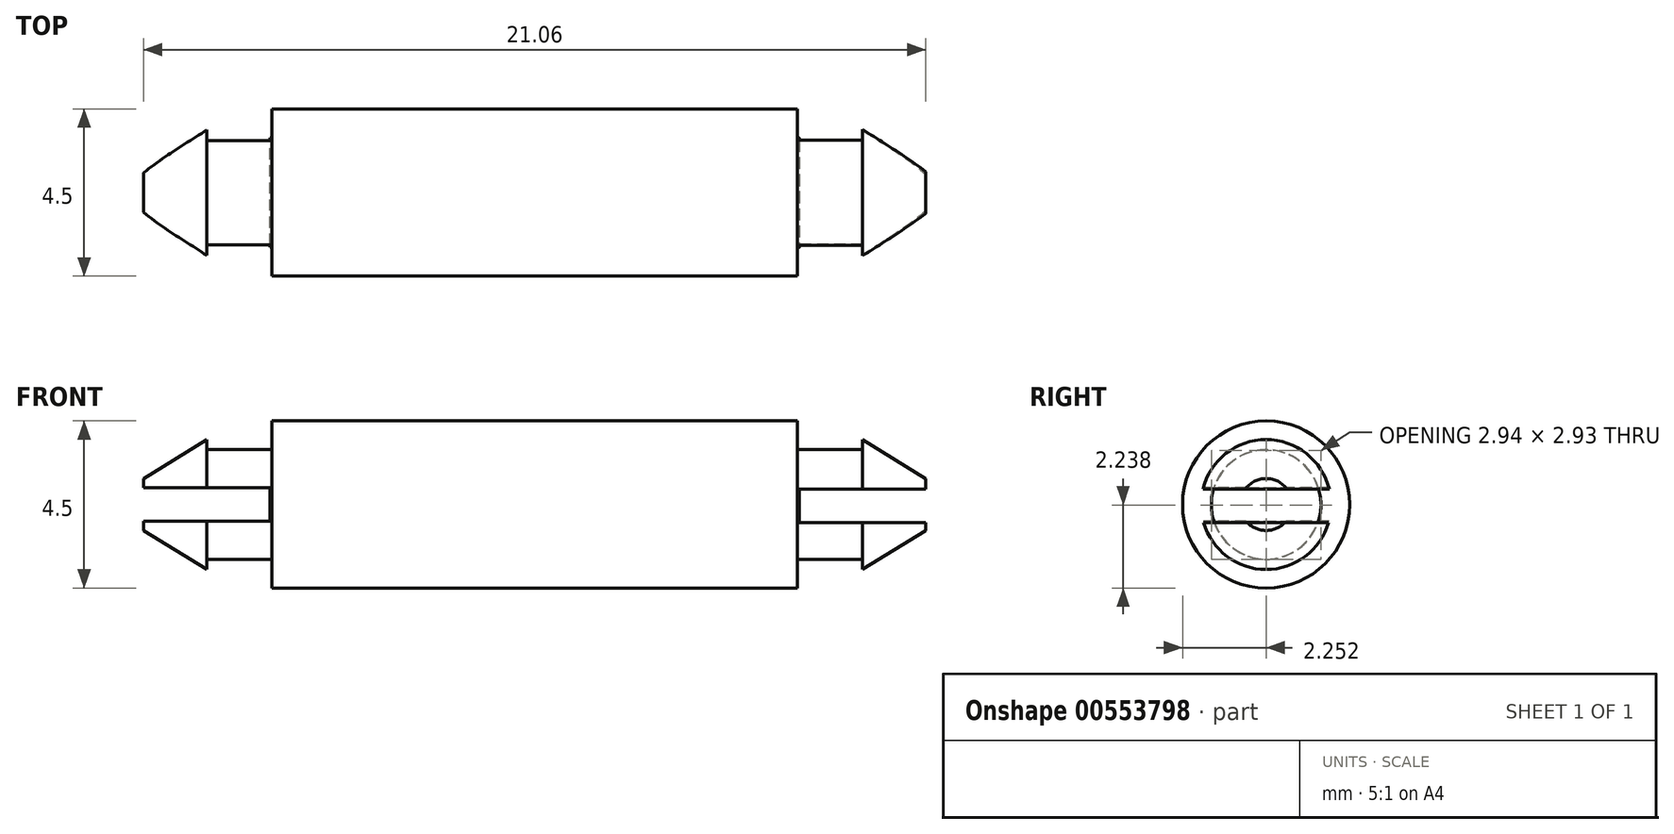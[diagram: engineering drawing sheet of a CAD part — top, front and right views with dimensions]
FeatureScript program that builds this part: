
annotation { "Feature Type Name" : "Feature", "Feature Type Description" : "" }
export const myFeature = defineFeature(function(context is Context, id is Id, definition is map)
    precondition{}
    {
        {
            var Q0;
            Q0=qCreatedBy(makeId("Right.planeOp"),FACE);
            var sketch = newSketch(context, id + "F0", { "sketchPlane" : qUnion([Q0])});
            skCircle(sketch, "E0", {"center": v(0, 0) * mm, "radius": 2.25 * mm});
            skCircle(sketch, "E1", {"center": v(0, 0) * mm, "radius": 1.48 * mm});
            skSolve(sketch);
        }
        {
            var Q0;
            Q0=makeQuery(id+"F0.imprint","IMPRINT",FACE,{"disambiguationData":[TD([[makeQuery(id+"F0.imprint","IMPRINT",EDGE,{"derivedFrom":sQuery(id+"F0.wireOp",EDGE,"E0")}),1.0]])]});
            var Q1;
            Q1 = qSketchRegion(id + "FBEnAiZPMkB544y_1", true);
            extrude(context, id + "F1", {"entities" : qUnion([Q0, Q1]), "endBound" : BoundingType.SYMMETRIC, "depth" : 14.15 * mm, "offsetDistance" : 25 * mm});
        }
        {
            var Q0;
            Q0=makeQuery(id+"F0.imprint","IMPRINT",FACE,{"disambiguationData":[TD([[makeQuery(id+"F0.imprint","IMPRINT",EDGE,{"derivedFrom":sQuery(id+"F0.wireOp",EDGE,"E1")}),1.0]])]});
            extrude(context, id + "F2", {"entities" : qUnion([Q0]), "operationType" : NewBodyOperationType.ADD, "endBound" : BoundingType.SYMMETRIC, "depth" : 17.65 * mm, "offsetDistance" : 25 * mm});
        }
        {
            var Q0;
            Q0=qCreatedBy(makeId("Front.planeOp"),FACE);
            var sketch = newSketch(context, id + "F3", { "sketchPlane" : qUnion([Q0])});
            skLineSegment(sketch, "E2", {"start": v(8.83, 0) * mm, "end": v(8.83, 1.75) * mm});
            skLineSegment(sketch, "E3", {"start": v(8.83, 1.75) * mm, "end": v(10.53, 0.7) * mm});
            skLineSegment(sketch, "E4", {"start": v(10.53, 0.7) * mm, "end": v(10.53, 0) * mm});
            skLineSegment(sketch, "E5", {"start": v(10.53, 0) * mm, "end": v(8.83, 0) * mm});
            skLineSegment(sketch, "E6", {"start": v(-8.82, 0) * mm, "end": v(-8.82, 1.75) * mm});
            skLineSegment(sketch, "E7", {"start": v(-8.82, 1.75) * mm, "end": v(-10.53, 0.7) * mm});
            skLineSegment(sketch, "E8", {"start": v(-10.53, 0.7) * mm, "end": v(-10.53, 0) * mm});
            skLineSegment(sketch, "E9", {"start": v(-10.53, 0) * mm, "end": v(-8.82, 0) * mm});
            skSolve(sketch);
        }
        {
            var Q0;
            Q0=makeQuery(id+"F3.imprint","IMPRINT",FACE,{"disambiguationData":[TD([[makeQuery(id+"F3.imprint","IMPRINT",EDGE,{"derivedFrom":sQuery(id+"F3.wireOp",EDGE,"E2")}),-1.0]])]});
            var Q1;
            Q1=makeQuery(id+"F3.imprint","IMPRINT",FACE,{"disambiguationData":[TD([[makeQuery(id+"F3.imprint","IMPRINT",EDGE,{"derivedFrom":sQuery(id+"F3.wireOp",EDGE,"E6")}),1.0]])]});
            var Q2;
            Q2=makeQuery(id+"F2.opExtrude","CAP_EDGE",EDGE,{"disambiguationData":[OSD([sQuery(id+"F0.wireOp",EDGE,"E1")])],"isStart":true});
            revolve(context, id + "F4", {"operationType" : NewBodyOperationType.ADD, "entities" : qUnion([Q0, Q1]), "axis" : qUnion([Q2]), "revolveType" : RevolveType.FULL});
        }
        {
            var Q0;
            Q0=makeQuery(id+"F4.opRevolve","SWEPT_FACE",FACE,{"disambiguationData":[OSD([sQuery(id+"F3.wireOp",EDGE,"E8")])]});
            var sketch = newSketch(context, id + "F5", { "sketchPlane" : qUnion([Q0])});
            skLineSegment(sketch, "E10.bottom", {"start": v(2.29, 0.45) * mm, "end": v(-2.29, 0.45) * mm});
            skLineSegment(sketch, "E10.top", {"start": v(2.29, -0.45) * mm, "end": v(-2.29, -0.45) * mm});
            skLineSegment(sketch, "E10.left", {"start": v(2.29, 0.45) * mm, "end": v(2.29, -0.45) * mm});
            skLineSegment(sketch, "E10.right", {"start": v(-2.29, 0.45) * mm, "end": v(-2.29, -0.45) * mm});
            skPoint(sketch, "E10.middle", {"position": v(0, 0) * mm});
            skSolve(sketch);
        }
        {
            var Q0;
            Q0 = qSketchRegion(id + "F5", true);
            extrude(context, id + "F6", {"entities" : qUnion([Q0]), "operationType" : NewBodyOperationType.REMOVE, "oppositeDirection" : true, "depth" : 3.4 * mm, "offsetDistance" : 25 * mm});
        }
        {
            var Q0;
            Q0=makeQuery(id+"F4.opRevolve","SWEPT_FACE",FACE,{"disambiguationData":[OSD([sQuery(id+"F3.wireOp",EDGE,"E4")])]});
            var sketch = newSketch(context, id + "F7", { "sketchPlane" : qUnion([Q0])});
            skLineSegment(sketch, "E11.bottom", {"start": v(3.24, 0.41) * mm, "end": v(-3.16, 0.41) * mm});
            skLineSegment(sketch, "E11.top", {"start": v(3.24, -0.49) * mm, "end": v(-3.16, -0.49) * mm});
            skLineSegment(sketch, "E11.left", {"start": v(3.24, 0.41) * mm, "end": v(3.24, -0.49) * mm});
            skLineSegment(sketch, "E11.right", {"start": v(-3.16, 0.41) * mm, "end": v(-3.16, -0.49) * mm});
            skPoint(sketch, "E11.middle", {"position": v(0.04, -0.04) * mm});
            skSolve(sketch);
        }
        {
            var Q0;
            Q0 = qSketchRegion(id + "F7", true);
            extrude(context, id + "F8", {"entities" : qUnion([Q0]), "operationType" : NewBodyOperationType.REMOVE, "oppositeDirection" : true, "depth" : 3.4 * mm, "offsetDistance" : 25 * mm});
        }
    });
